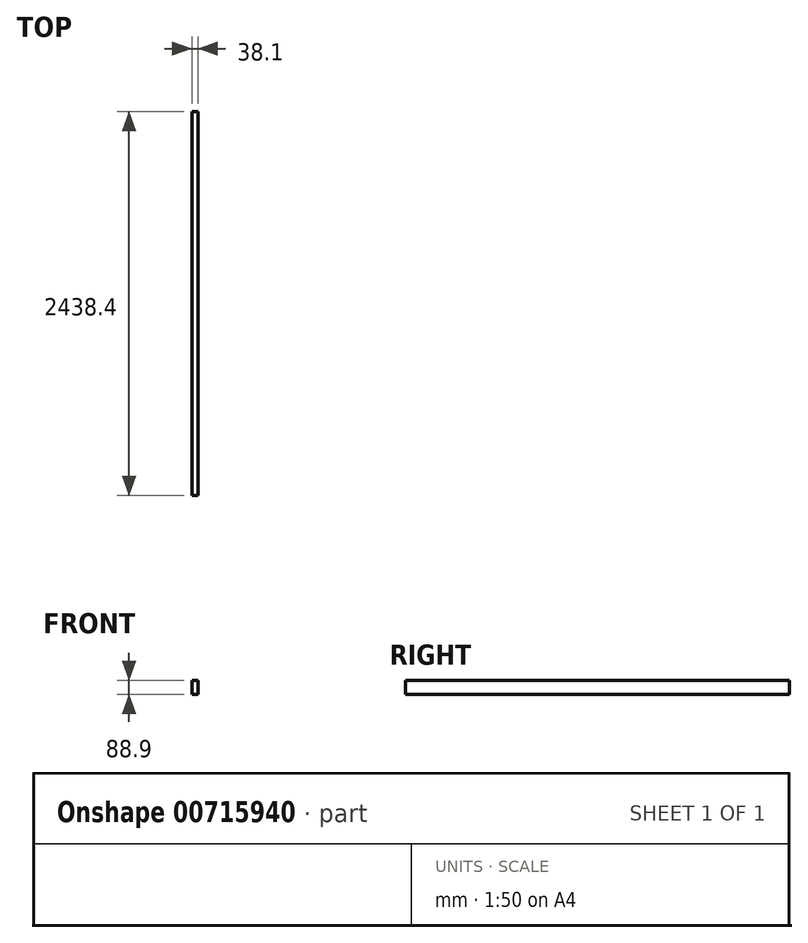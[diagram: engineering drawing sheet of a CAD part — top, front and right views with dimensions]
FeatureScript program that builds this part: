
annotation { "Feature Type Name" : "Feature", "Feature Type Description" : "" }
export const myFeature = defineFeature(function(context is Context, id is Id, definition is map)
    precondition{}
    {
        {
            var Q0;
            Q0=qCreatedBy(makeId("Front.planeOp"),FACE);
            var sketch = newSketch(context, id + "F0", { "sketchPlane" : qUnion([Q0])});
            skLineSegment(sketch, "E0.bottom", {"start": v(-19.05, 44.45) * mm, "end": v(19.05, 44.45) * mm});
            skLineSegment(sketch, "E0.top", {"start": v(-19.05, -44.45) * mm, "end": v(19.05, -44.45) * mm});
            skLineSegment(sketch, "E0.left", {"start": v(-19.05, 44.45) * mm, "end": v(-19.05, -44.45) * mm});
            skLineSegment(sketch, "E0.right", {"start": v(19.05, 44.45) * mm, "end": v(19.05, -44.45) * mm});
            skPoint(sketch, "E0.middle", {"position": v(0, 0) * mm});
            skSolve(sketch);
        }
        {
            var Q0;
            Q0=makeQuery(id+"F0.imprint","IMPRINT",FACE,{"disambiguationData":[TD([[makeQuery(id+"F0.imprint","IMPRINT",EDGE,{"derivedFrom":sQuery(id+"F0.wireOp",EDGE,"E0.bottom")}),-1.0]])]});
            extrude(context, id + "F1", {"entities" : qUnion([Q0]), "endBound" : BoundingType.SYMMETRIC, "depth" : 2438.4 * mm, "offsetDistance" : 25.4 * mm});
        }
    });
